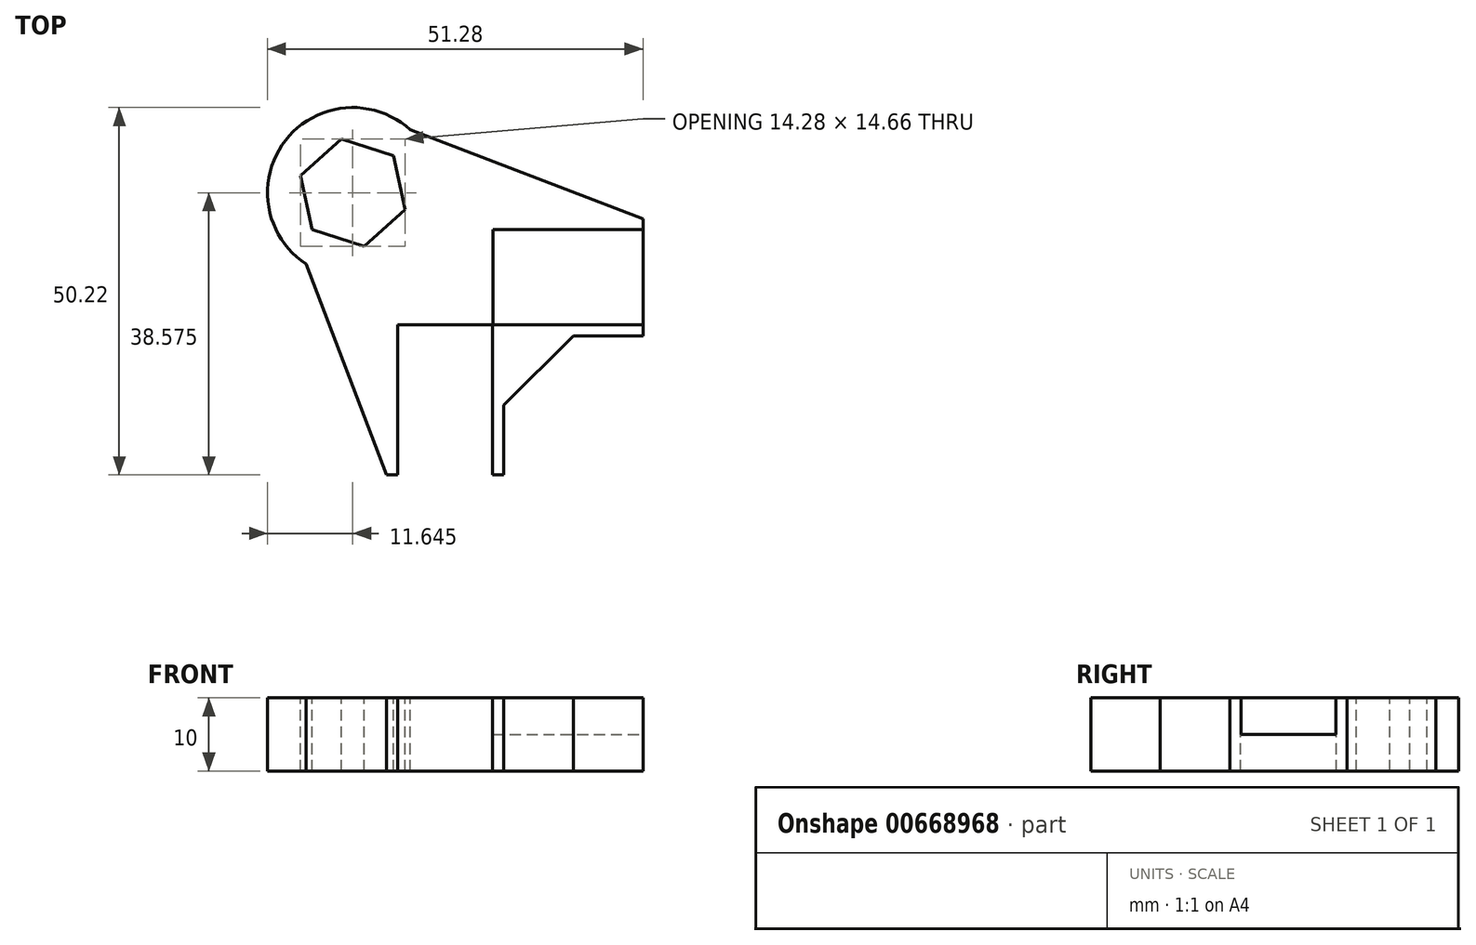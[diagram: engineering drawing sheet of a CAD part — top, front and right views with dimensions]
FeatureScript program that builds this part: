
annotation { "Feature Type Name" : "Feature", "Feature Type Description" : "" }
export const myFeature = defineFeature(function(context is Context, id is Id, definition is map)
    precondition{}
    {
        {
            var Q0;
            Q0=qCreatedBy(makeId("Top.planeOp"),FACE);
            var sketch = newSketch(context, id + "F0", { "sketchPlane" : qUnion([Q0])});
            skLineSegment(sketch, "E0", {"start": v(-54.9, 0) * mm, "end": v(-54.9, 20.59) * mm});
            skLineSegment(sketch, "E1", {"start": v(-19.9, 35) * mm, "end": v(-19.9, 19) * mm});
            skLineSegment(sketch, "E2", {"start": v(-19.9, 19) * mm, "end": v(-38.9, 19) * mm});
            skLineSegment(sketch, "E3", {"start": v(-38.9, 19) * mm, "end": v(-38.9, 0) * mm});
            skLineSegment(sketch, "E4", {"start": v(-38.9, 0) * mm, "end": v(-54.9, 0) * mm});
            skLineSegment(sketch, "E5.bottom", {"start": v(-52.13, 0) * mm, "end": v(-40.32, 0) * mm});
            skLineSegment(sketch, "E6.bottom", {"start": v(-40.37, 33.5) * mm, "end": v(-19.87, 33.5) * mm});
            skLineSegment(sketch, "E6.top", {"start": v(-40.37, 20.5) * mm, "end": v(-19.87, 20.5) * mm});
            skLineSegment(sketch, "E6.left", {"start": v(-40.37, 33.5) * mm, "end": v(-40.37, 20.5) * mm});
            skLineSegment(sketch, "E6.right", {"start": v(-19.87, 33.5) * mm, "end": v(-19.87, 20.5) * mm});
            skLineSegment(sketch, "E7", {"start": v(-29.4, 19) * mm, "end": v(-38.9, 9.5) * mm});
            skCircle(sketch, "E8.cCircle", {"center": v(-59.54, 38.57) * mm, "radius": 6.5 * mm, "construction": true});
            skLineSegment(sketch, "E8.0", {"start": v(-61.12, 45.9) * mm, "end": v(-53.98, 43.6) * mm});
            skLineSegment(sketch, "E8.1", {"start": v(-53.98, 43.6) * mm, "end": v(-52.4, 36.28) * mm});
            skLineSegment(sketch, "E8.2", {"start": v(-52.4, 36.28) * mm, "end": v(-57.95, 31.24) * mm});
            skLineSegment(sketch, "E8.3", {"start": v(-57.95, 31.24) * mm, "end": v(-65.1, 33.54) * mm});
            skLineSegment(sketch, "E8.4", {"start": v(-65.1, 33.54) * mm, "end": v(-66.67, 40.87) * mm});
            skLineSegment(sketch, "E8.5", {"start": v(-66.67, 40.87) * mm, "end": v(-61.12, 45.9) * mm});
            skPoint(sketch, "E8.0.midPoint", {"position": v(-57.55, 44.76) * mm});
            skLineSegment(sketch, "E9.trimOffspring", {"start": v(-40.44, 35) * mm, "end": v(-19.9, 35) * mm});
            skLineSegment(sketch, "E10.bottom", {"start": v(-53.43, 20.48) * mm, "end": v(-40.43, 20.48) * mm});
            skLineSegment(sketch, "E10.top", {"start": v(-53.43, -0.02) * mm, "end": v(-40.43, -0.02) * mm});
            skLineSegment(sketch, "E10.left", {"start": v(-53.43, 20.48) * mm, "end": v(-53.43, -0.02) * mm});
            skLineSegment(sketch, "E10.right", {"start": v(-40.43, 20.48) * mm, "end": v(-40.43, -0.02) * mm});
            skLineSegment(sketch, "E11", {"start": v(-40.37, 33.5) * mm, "end": v(-53.57, 33.5) * mm, "construction": true});
            skLineSegment(sketch, "E12", {"start": v(-53.43, 20.48) * mm, "end": v(-53.43, 39.13) * mm, "construction": true});
            skArc(sketch, "E13", {"start": v(-51.67, 47.16) * mm, "mid": v(-68.73, 45.72) * mm, "end": v(-65.9, 28.83) * mm});
            skLineSegment(sketch, "E14", {"start": v(-65.9, 28.83) * mm, "end": v(-54.9, 0) * mm});
            skLineSegment(sketch, "E15", {"start": v(-51.67, 47.16) * mm, "end": v(-19.9, 35) * mm});
            skSolve(sketch);
        }
        {
            var Q0;
            {var subQ10=sQuery(id+"F0.wireOp",EDGE,"5TOnWfzQ-x5ts-Ff0P-cbdN-hFC0nQrYrY2S");Q0=makeQuery(id+"F0.imprint","IMPRINT",FACE,{"disambiguationData":[TD([[makeQuery(id+"F0.imprint","IMPRINT",EDGE,{"derivedFrom":subQ10}),1.0]])]});}
            var Q1;
            {var subQ0=sQuery(id+"F0.wireOp",EDGE,"E5.left");Q1=makeQuery(id+"F0.imprint","IMPRINT",FACE,{"disambiguationData":[TD([[makeQuery(id+"F0.imprint","IMPRINT",EDGE,{"derivedFrom":subQ0}),1.0]])]});}
            var Q2;
            {var subQ1=sQuery(id+"F0.wireOp",EDGE,"E5.bottom");Q2=makeQuery(id+"F0.imprint","IMPRINT",FACE,{"disambiguationData":[TD([[makeQuery(id+"F0.imprint","IMPRINT",EDGE,{"derivedFrom":subQ1}),1.0]])]});}
            var Q3;
            {var subQ0=sQuery(id+"F0.wireOp",EDGE,"E5.right");var subQ1=sQuery(id+"F0.wireOp",EDGE,"E5.top");var subQ2=makeQuery(id+"F0.imprint","INTERSECT",VERTEX,{"derivedFrom":[subQ1,subQ0]});Q3=makeQuery(id+"F0.imprint","IMPRINT",FACE,{"disambiguationData":[TD([[makeQuery(id+"F0.imprint","IMPRINT",EDGE,{"disambiguationData":[TD([[subQ2,1.0]])],"derivedFrom":subQ1}),-1.0]])]});}
            var Q4;
            {var subQ1=sQuery(id+"F0.wireOp",EDGE,"E6.bottom");var subQ3=sQuery(id+"F0.wireOp",EDGE,"E1");var subQ4=makeQuery(id+"F0.imprint","INTERSECT",VERTEX,{"derivedFrom":[subQ3,subQ1]});Q4=makeQuery(id+"F0.imprint","IMPRINT",FACE,{"disambiguationData":[TD([[makeQuery(id+"F0.imprint","IMPRINT",EDGE,{"disambiguationData":[TD([[subQ4,-1.0]])],"derivedFrom":subQ3}),-1.0]])]});}
            var Q5;
            {var subQ1=sQuery(id+"F0.wireOp",EDGE,"E2");var subQ6=sQuery(id+"F0.wireOp",EDGE,"E1");var subQ7=makeQuery(id+"F0.imprint","INTERSECT",VERTEX,{"derivedFrom":[subQ6,subQ1]});Q5=makeQuery(id+"F0.imprint","IMPRINT",FACE,{"disambiguationData":[TD([[makeQuery(id+"F0.imprint","IMPRINT",EDGE,{"disambiguationData":[TD([[subQ7,1.0]])],"derivedFrom":subQ6}),-1.0]])]});}
            var Q6;
            {var subQ3=sQuery(id+"F0.wireOp",EDGE,"E7");Q6=makeQuery(id+"F0.imprint","IMPRINT",FACE,{"disambiguationData":[TD([[makeQuery(id+"F0.imprint","IMPRINT",EDGE,{"derivedFrom":subQ3}),-1.0]])]});}
            var Q7;
            {var subQ0=sQuery(id+"F0.wireOp",EDGE,"OypnBC8w-5hva-jbQl-pIpI-49nbCExjwXDB");var subQ1=sQuery(id+"F0.wireOp",EDGE,"E0");var subQ2=makeQuery(id+"F0.imprint","INTERSECT",VERTEX,{"derivedFrom":[subQ1,subQ0]});Q7=makeQuery(id+"F0.imprint","IMPRINT",FACE,{"disambiguationData":[TD([[makeQuery(id+"F0.imprint","IMPRINT",EDGE,{"disambiguationData":[TD([[subQ2,1.0]])],"derivedFrom":subQ1}),-1.0]])]});}
            extrude(context, id + "F1", {"entities" : qUnion([Q0, Q1, Q2, Q3, Q4, Q5, Q6, Q7]), "oppositeDirection" : true, "depth" : 10 * mm, "offsetDistance" : 25 * mm});
        }
        {
            var Q0;
            Q0=makeQuery(id+"F0.imprint","IMPRINT",FACE,{"disambiguationData":[TD([[makeQuery(id+"F0.imprint","IMPRINT",EDGE,{"derivedFrom":sQuery(id+"F0.wireOp",EDGE,"E5.bottom")}),1.0]])]});
            var Q1;
            Q1=makeQuery(id+"F0.imprint","IMPRINT",FACE,{"disambiguationData":[TD([[makeQuery(id+"F0.imprint","IMPRINT",EDGE,{"derivedFrom":sQuery(id+"F0.wireOp",EDGE,"E6.bottom")}),-1.0]])]});
            var Q2;
            {var subQ1=sQuery(id+"F0.wireOp",EDGE,"E6.bottom");var subQ3=sQuery(id+"F0.wireOp",EDGE,"E1");var subQ4=makeQuery(id+"F0.imprint","INTERSECT",VERTEX,{"derivedFrom":[subQ3,subQ1]});Q2=makeQuery(id+"F0.imprint","IMPRINT",FACE,{"disambiguationData":[TD([[makeQuery(id+"F0.imprint","IMPRINT",EDGE,{"disambiguationData":[TD([[subQ4,-1.0]])],"derivedFrom":subQ3}),-1.0]])]});}
            var Q3;
            {var subQ0=sQuery(id+"F0.wireOp",EDGE,"E5.right");var subQ1=sQuery(id+"F0.wireOp",EDGE,"E5.top");var subQ2=makeQuery(id+"F0.imprint","INTERSECT",VERTEX,{"derivedFrom":[subQ1,subQ0]});Q3=makeQuery(id+"F0.imprint","IMPRINT",FACE,{"disambiguationData":[TD([[makeQuery(id+"F0.imprint","IMPRINT",EDGE,{"disambiguationData":[TD([[subQ2,1.0]])],"derivedFrom":subQ1}),-1.0]])]});}
            extrude(context, id + "F2", {"entities" : qUnion([Q0, Q1, Q2, Q3]), "operationType" : NewBodyOperationType.REMOVE, "oppositeDirection" : true, "depth" : 5 * mm, "offsetDistance" : 25 * mm});
        }
    });
